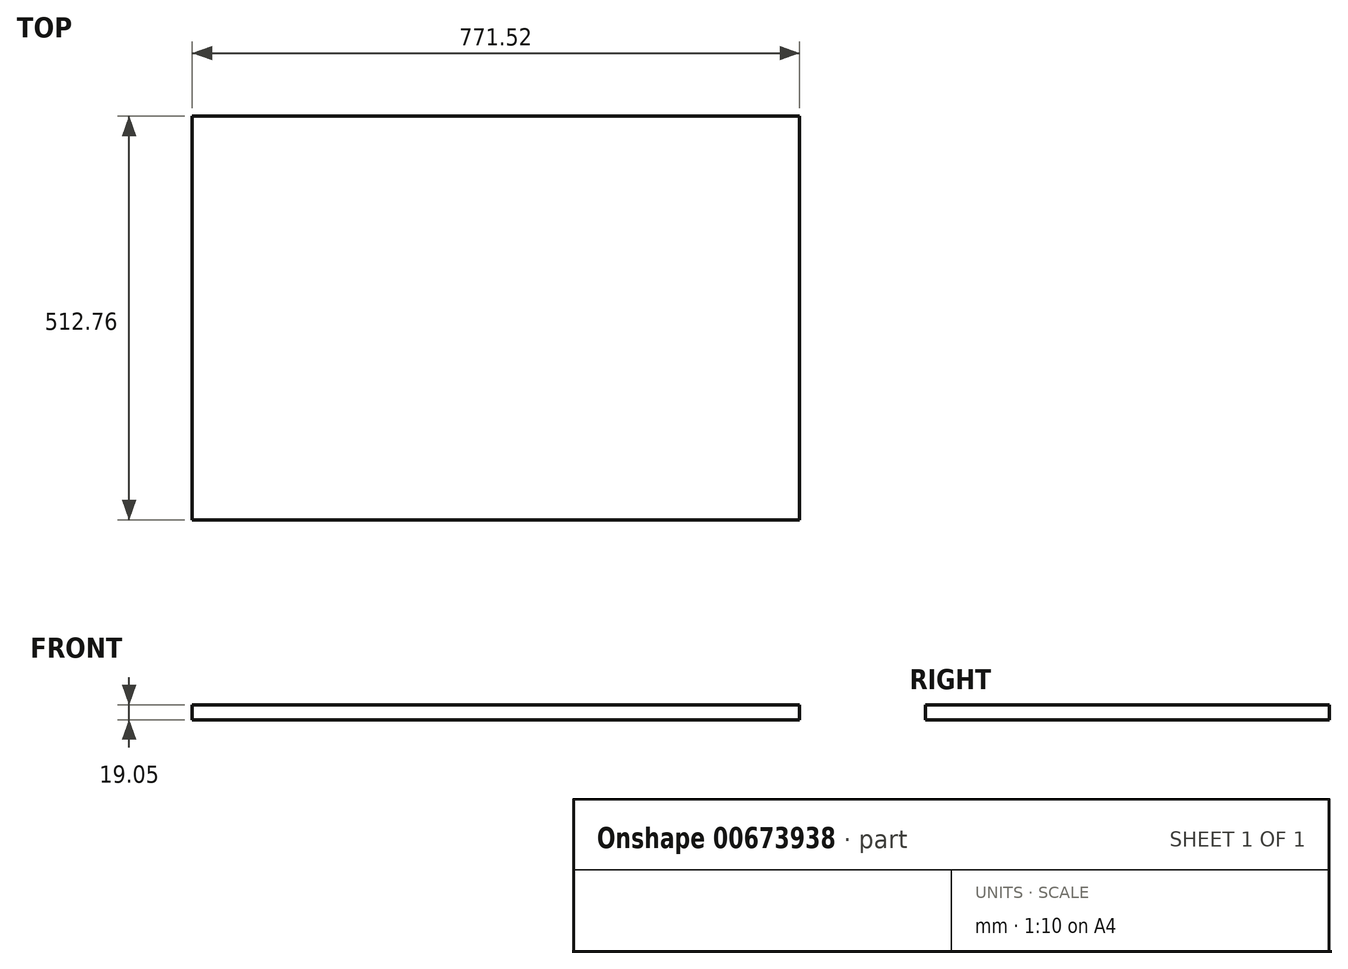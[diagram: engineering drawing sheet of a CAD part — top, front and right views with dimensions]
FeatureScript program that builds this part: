
annotation { "Feature Type Name" : "Feature", "Feature Type Description" : "" }
export const myFeature = defineFeature(function(context is Context, id is Id, definition is map)
    precondition{}
    {
        {
            var Q0;
            Q0=qCreatedBy(makeId("Top.planeOp"),FACE);
            var sketch = newSketch(context, id + "F0", { "sketchPlane" : qUnion([Q0])});
            skLineSegment(sketch, "E0.bottom", {"start": v(-381.48, 310.94) * mm, "end": v(390.04, 310.94) * mm});
            skLineSegment(sketch, "E0.top", {"start": v(-381.48, -201.82) * mm, "end": v(390.04, -201.82) * mm});
            skLineSegment(sketch, "E0.left", {"start": v(-381.48, 310.94) * mm, "end": v(-381.48, -201.82) * mm});
            skLineSegment(sketch, "E0.right", {"start": v(390.04, 310.94) * mm, "end": v(390.04, -201.82) * mm});
            skSolve(sketch);
        }
        {
            var Q0;
            Q0=makeQuery(id+"F0.imprint","IMPRINT",FACE,{"disambiguationData":[TD([[makeQuery(id+"F0.imprint","IMPRINT",EDGE,{"derivedFrom":sQuery(id+"F0.wireOp",EDGE,"E0.bottom")}),-1.0]])]});
            extrude(context, id + "F1", {"entities" : qUnion([Q0]), "depth" : 19.05 * mm, "offsetDistance" : 25.4 * mm});
        }
    });
